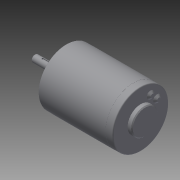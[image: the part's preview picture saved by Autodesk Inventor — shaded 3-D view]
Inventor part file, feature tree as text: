
AUTODESK INVENTOR PART (.ipt)
format: ipt  version: 2013 SP1 (Build 170176100, 176)  size: 148,480 bytes
history: native  units: in
note: dims shown in document units (in); Inventor stores cm internally (conversion verified against a paired STEP export)
features: chamfer x1, imported_body x1
ambient origin geometry x8: Origin, YZ Plane, XZ Plane, XY Plane, X Axis, Y Axis, Z Axis, Center Point
feature tree (2):
  chamfer  "Chamfer3"  [1 undecoded]
  imported_body  "Base1"
note: 1 required parameter value undecoded (feature->parameter linkage not recoverable at this tier; creation-order binding heuristic only, values carry confidence <= 0.55)
